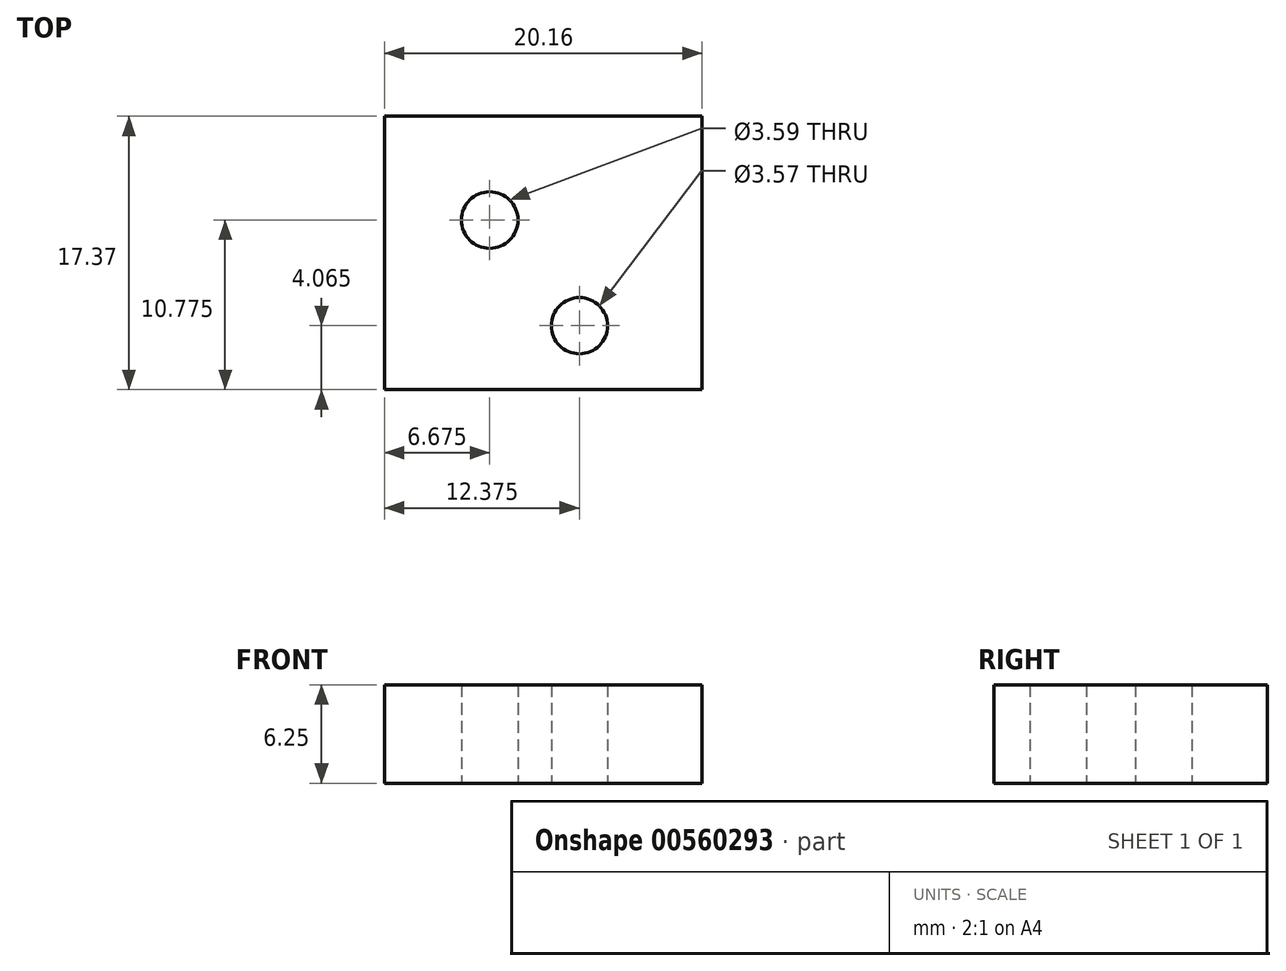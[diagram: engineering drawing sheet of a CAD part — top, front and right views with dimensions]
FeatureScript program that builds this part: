
annotation { "Feature Type Name" : "Feature", "Feature Type Description" : "" }
export const myFeature = defineFeature(function(context is Context, id is Id, definition is map)
    precondition{}
    {
        {
            var Q0;
            Q0=qCreatedBy(makeId("Top.planeOp"),FACE);
            var sketch = newSketch(context, id + "F0", { "sketchPlane" : qUnion([Q0])});
            skLineSegment(sketch, "E0.bottom", {"start": v(0, 17.37) * mm, "end": v(20.16, 17.37) * mm});
            skLineSegment(sketch, "E0.top", {"start": v(0, 0) * mm, "end": v(20.16, 0) * mm});
            skLineSegment(sketch, "E0.left", {"start": v(0, 17.37) * mm, "end": v(0, 0) * mm});
            skLineSegment(sketch, "E0.right", {"start": v(20.16, 17.37) * mm, "end": v(20.16, 0) * mm});
            skCircle(sketch, "E1", {"center": v(6.68, 10.78) * mm, "radius": 1.8 * mm});
            skCircle(sketch, "E2", {"center": v(12.38, 4.07) * mm, "radius": 1.78 * mm});
            skSolve(sketch);
        }
        {
            var Q0;
            Q0=makeQuery(id+"F0.imprint","IMPRINT",FACE,{"disambiguationData":[TD([[makeQuery(id+"F0.imprint","IMPRINT",EDGE,{"derivedFrom":sQuery(id+"F0.wireOp",EDGE,"E0.bottom")}),-1.0]])]});
            extrude(context, id + "F1", {"entities" : qUnion([Q0]), "depth" : 6.25 * mm, "offsetDistance" : 25 * mm});
        }
    });
